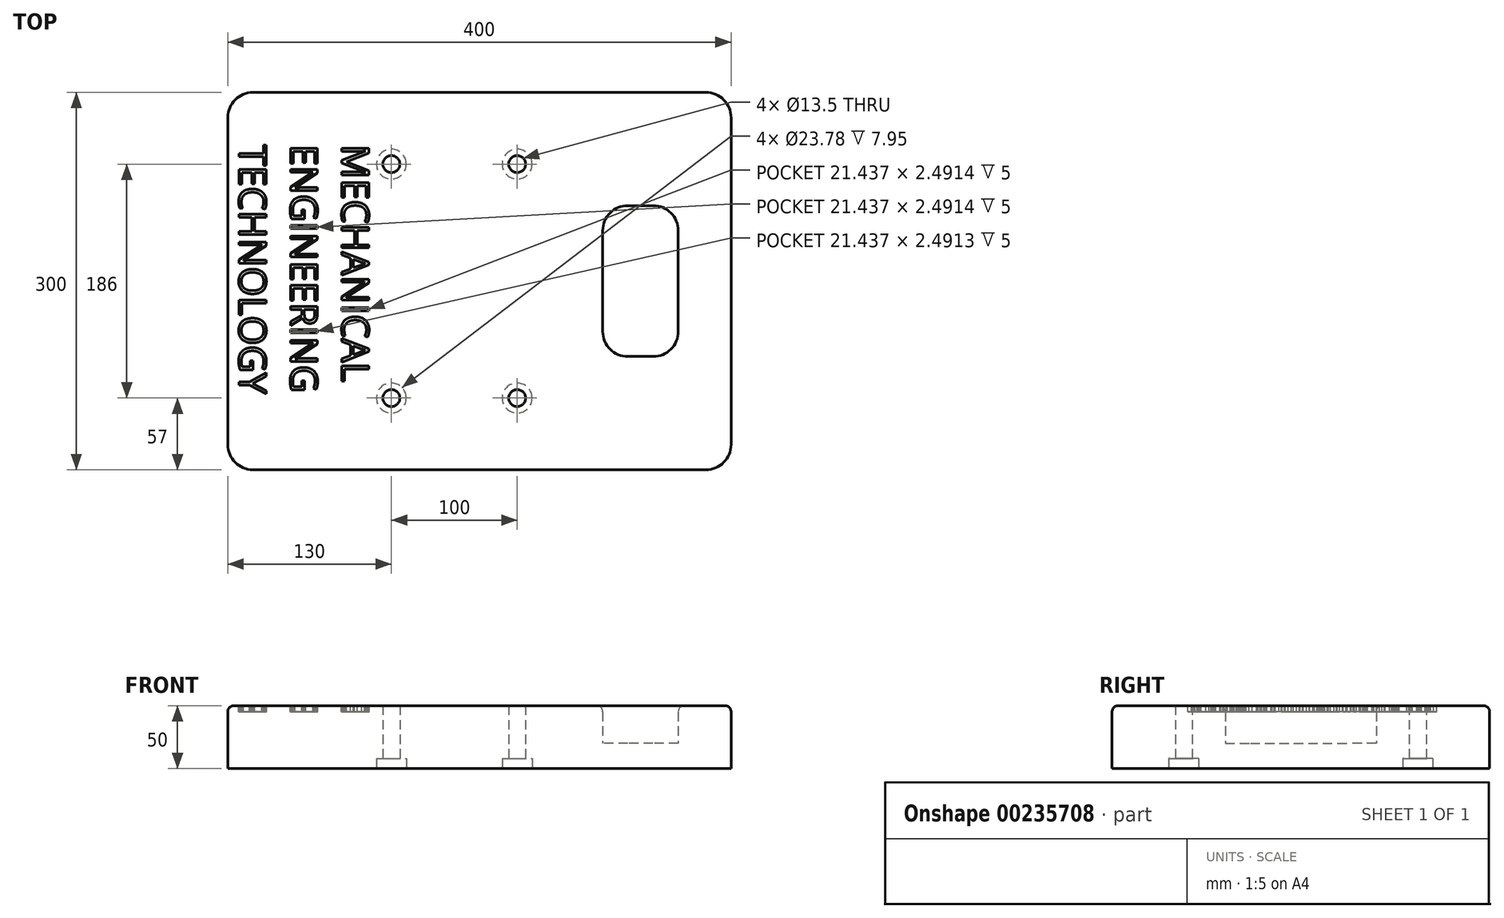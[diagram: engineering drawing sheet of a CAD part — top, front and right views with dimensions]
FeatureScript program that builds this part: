
annotation { "Feature Type Name" : "Feature", "Feature Type Description" : "" }
export const myFeature = defineFeature(function(context is Context, id is Id, definition is map)
    precondition{}
    {
        {
            var Q0;
            Q0=qCreatedBy(makeId("Top.planeOp"),FACE);
            var sketch = newSketch(context, id + "F0", { "sketchPlane" : qUnion([Q0])});
            skLineSegment(sketch, "E0.bottom", {"start": v(180, -150) * mm, "end": v(-180, -150) * mm});
            skLineSegment(sketch, "E0.top", {"start": v(180, 150) * mm, "end": v(-180, 150) * mm});
            skLineSegment(sketch, "E0.left", {"start": v(200, -130) * mm, "end": v(200, 130) * mm});
            skLineSegment(sketch, "E0.right", {"start": v(-200, -130) * mm, "end": v(-200, 130) * mm});
            skPoint(sketch, "E0.middle", {"position": v(0, 0) * mm});
            skLineSegment(sketch, "E1", {"start": v(-200, 0) * mm, "end": v(128, 0) * mm, "construction": true});
            skLineSegment(sketch, "E2.bottom", {"start": v(138, -60) * mm, "end": v(118, -60) * mm});
            skLineSegment(sketch, "E2.top", {"start": v(138, 60) * mm, "end": v(118, 60) * mm});
            skLineSegment(sketch, "E2.left", {"start": v(158, -40) * mm, "end": v(158, 40) * mm});
            skLineSegment(sketch, "E2.right", {"start": v(98, -40) * mm, "end": v(98, 40) * mm});
            skPoint(sketch, "E2.middle", {"position": v(128, 0) * mm});
            skLineSegment(sketch, "E3", {"start": v(200, 0) * mm, "end": v(30, 0) * mm, "construction": true});
            skLineSegment(sketch, "E4", {"start": v(30, 0) * mm, "end": v(30, -93) * mm, "construction": true});
            skLineSegment(sketch, "E5.bottom", {"start": v(30, -93) * mm, "end": v(-70, -93) * mm, "construction": true});
            skLineSegment(sketch, "E5.top", {"start": v(30, 93) * mm, "end": v(-70, 93) * mm, "construction": true});
            skLineSegment(sketch, "E5.left", {"start": v(30, 0) * mm, "end": v(30, 93) * mm, "construction": true});
            skLineSegment(sketch, "E5.right", {"start": v(-70, -93) * mm, "end": v(-70, 93) * mm, "construction": true});
            skPoint(sketch, "E6.visualSharp", {"position": v(158, 60) * mm});
            skArc(sketch, "E6.filletArc", {"start": v(158, 40) * mm, "mid": v(152.14, 54.14) * mm, "end": v(138, 60) * mm});
            skPoint(sketch, "E7.visualSharp", {"position": v(98, 60) * mm});
            skArc(sketch, "E7.filletArc", {"start": v(118, 60) * mm, "mid": v(103.86, 54.14) * mm, "end": v(98, 40) * mm});
            skPoint(sketch, "E8.visualSharp", {"position": v(98, -60) * mm});
            skArc(sketch, "E8.filletArc", {"start": v(98, -40) * mm, "mid": v(103.86, -54.14) * mm, "end": v(118, -60) * mm});
            skPoint(sketch, "E9.visualSharp", {"position": v(158, -60) * mm});
            skArc(sketch, "E9.filletArc", {"start": v(138, -60) * mm, "mid": v(152.14, -54.14) * mm, "end": v(158, -40) * mm});
            skPoint(sketch, "E10.visualSharp", {"position": v(-200, 150) * mm});
            skArc(sketch, "E10.filletArc", {"start": v(-180, 150) * mm, "mid": v(-194.14, 144.14) * mm, "end": v(-200, 130) * mm});
            skPoint(sketch, "E11.visualSharp", {"position": v(200, 150) * mm});
            skArc(sketch, "E11.filletArc", {"start": v(200, 130) * mm, "mid": v(194.14, 144.14) * mm, "end": v(180, 150) * mm});
            skPoint(sketch, "E12.visualSharp", {"position": v(200, -150) * mm});
            skArc(sketch, "E12.filletArc", {"start": v(180, -150) * mm, "mid": v(194.14, -144.14) * mm, "end": v(200, -130) * mm});
            skPoint(sketch, "E13.visualSharp", {"position": v(-200, -150) * mm});
            skArc(sketch, "E13.filletArc", {"start": v(-200, -130) * mm, "mid": v(-194.14, -144.14) * mm, "end": v(-180, -150) * mm});
            skSolve(sketch);
        }
        {
            var Q0;
            Q0=makeQuery(id+"F0.imprint","IMPRINT",FACE,{"disambiguationData":[TD([[makeQuery(id+"F0.imprint","IMPRINT",EDGE,{"derivedFrom":sQuery(id+"F0.wireOp",EDGE,"E0.bottom")}),-1.0]])]});
            extrude(context, id + "F1", {"entities" : qUnion([Q0]), "depth" : 50 * mm});
        }
        {
            var Q0;
            Q0=makeQuery(id+"F0.imprint","IMPRINT",FACE,{"disambiguationData":[TD([[makeQuery(id+"F0.imprint","IMPRINT",EDGE,{"derivedFrom":sQuery(id+"F0.wireOp",EDGE,"E2.bottom")}),-1.0]])]});
            extrude(context, id + "F2", {"entities" : qUnion([Q0]), "operationType" : NewBodyOperationType.ADD, "depth" : 20 * mm});
        }
        {
            var Q0;
            Q0=sQuery(id+"F0.wireOp",VERTEX,"E5.right.start");
            var Q1;
            Q1=sQuery(id+"F0.wireOp",VERTEX,"E5.bottom.start");
            var Q2;
            Q2=sQuery(id+"F0.wireOp",VERTEX,"E5.top.start");
            var Q3;
            Q3=sQuery(id+"F0.wireOp",VERTEX,"E5.top.end");
            var Q4;
            Q4=makeQuery(id+"F1.opExtrude","SWEPT_BODY",BODY,{"disambiguationData":[OSD([sQuery(id+"F0.wireOp",EDGE,"E0.bottom"),sQuery(id+"F0.wireOp",EDGE,"E0.top"),sQuery(id+"F0.wireOp",EDGE,"E0.left"),sQuery(id+"F0.wireOp",EDGE,"E0.right"),sQuery(id+"F0.wireOp",EDGE,"E2.bottom"),sQuery(id+"F0.wireOp",EDGE,"E2.top"),sQuery(id+"F0.wireOp",EDGE,"E2.left"),sQuery(id+"F0.wireOp",EDGE,"E2.right"),sQuery(id+"F0.wireOp",EDGE,"E6.filletArc"),sQuery(id+"F0.wireOp",EDGE,"E7.filletArc"),sQuery(id+"F0.wireOp",EDGE,"E8.filletArc"),sQuery(id+"F0.wireOp",EDGE,"E9.filletArc"),sQuery(id+"F0.wireOp",EDGE,"E10.filletArc"),sQuery(id+"F0.wireOp",EDGE,"E11.filletArc"),sQuery(id+"F0.wireOp",EDGE,"E12.filletArc"),sQuery(id+"F0.wireOp",EDGE,"E13.filletArc")])]});
            hole(context, id + "F3", {"style" : HoleStyle.C_BORE, "endStyle" : HoleEndStyle.THROUGH, "oppositeDirection" : true, "holeDiameter" : 13.5 * mm, "cBoreDiameter" : 23.78 * mm, "cBoreDepth" : 7.95 * mm, "tappedDepth" : 9 * mm, "tapClearance" : 3, "startFromSketch" : true, "locations" : qUnion([Q0, Q1, Q2, Q3]), "scope" : qUnion([Q4])});
        }
        {
            var Q0;
            Q0=makeQuery(id+"F1.opExtrude","CAP_FACE",FACE,{"disambiguationData":[OSD([sQuery(id+"F0.wireOp",EDGE,"E0.bottom"),sQuery(id+"F0.wireOp",EDGE,"E0.top"),sQuery(id+"F0.wireOp",EDGE,"E0.left"),sQuery(id+"F0.wireOp",EDGE,"E0.right"),sQuery(id+"F0.wireOp",EDGE,"E2.bottom"),sQuery(id+"F0.wireOp",EDGE,"E2.top"),sQuery(id+"F0.wireOp",EDGE,"E2.left"),sQuery(id+"F0.wireOp",EDGE,"E2.right"),sQuery(id+"F0.wireOp",EDGE,"E6.filletArc"),sQuery(id+"F0.wireOp",EDGE,"E7.filletArc"),sQuery(id+"F0.wireOp",EDGE,"E8.filletArc"),sQuery(id+"F0.wireOp",EDGE,"E9.filletArc"),sQuery(id+"F0.wireOp",EDGE,"E10.filletArc"),sQuery(id+"F0.wireOp",EDGE,"E11.filletArc"),sQuery(id+"F0.wireOp",EDGE,"E12.filletArc"),sQuery(id+"F0.wireOp",EDGE,"E13.filletArc")])],"isStart":false});
            var sketch = newSketch(context, id + "F4", { "sketchPlane" : qUnion([Q0])});
            skText(sketch, "E14", { "text": "MECHANICAL\nENGINEERING \nTECHNOLOGY", "fontName": "OpenSans-Regular.ttf"});
            const initialGuessF4  = {"E14": [-0.10938, 0.10838, 0, -1, 0.02162]};
            skSetInitialGuess(sketch, initialGuessF4);
            skSolve(sketch);
        }
        {
            var Q0;
            Q0 = qSketchRegion(id + "F4", true);
            extrude(context, id + "F5", {"entities" : qUnion([Q0]), "operationType" : NewBodyOperationType.REMOVE, "oppositeDirection" : true, "depth" : 5 * mm});
        }
        {
            var Q0;
            Q0=makeQuery(id+"F1.opExtrude","CAP_EDGE",EDGE,{"disambiguationData":[OSD([sQuery(id+"F0.wireOp",EDGE,"E0.bottom")])],"isStart":false});
            var Q1;
            Q1=makeQuery(id+"F1.opExtrude","CAP_EDGE",EDGE,{"disambiguationData":[OSD([sQuery(id+"F0.wireOp",EDGE,"E2.left")])],"isStart":false});
            var Q2;
            Q2=makeQuery(id+"F2.opExtrude","CAP_EDGE",EDGE,{"disambiguationData":[OSD([sQuery(id+"F0.wireOp",EDGE,"E2.left")])],"isStart":false});
            fillet(context, id + "F6", {"entities" : qUnion([Q0, Q1, Q2]), "radius" : 5 * mm, "tangentPropagation" : true, "allowEdgeOverflow" : false});
        }
    });
